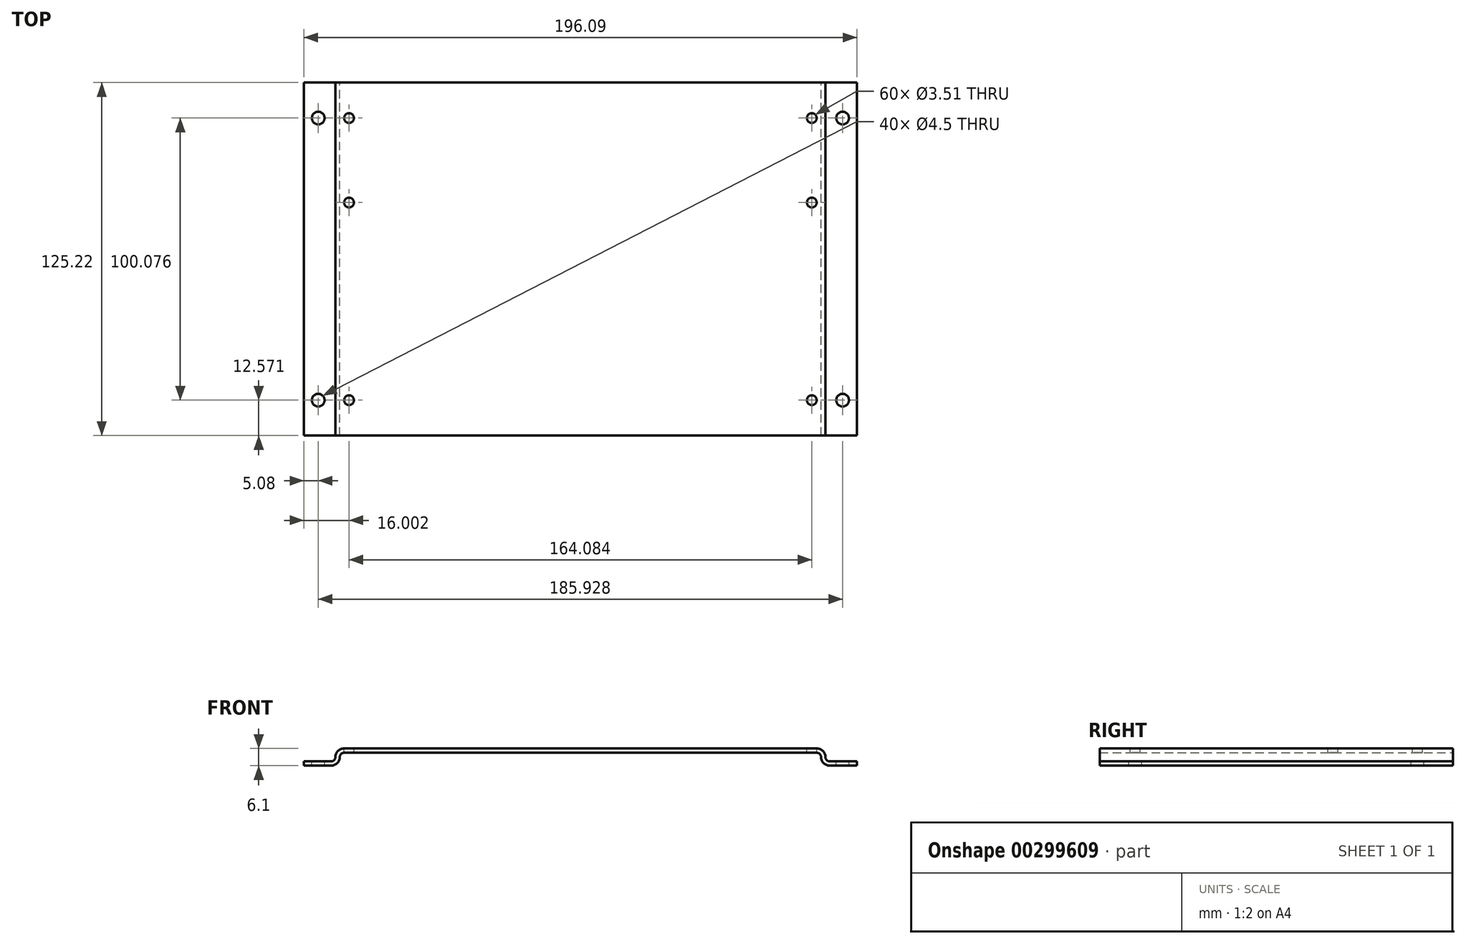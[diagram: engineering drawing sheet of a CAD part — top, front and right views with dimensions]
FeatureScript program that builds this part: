
annotation { "Feature Type Name" : "Feature", "Feature Type Description" : "" }
export const myFeature = defineFeature(function(context is Context, id is Id, definition is map)
    precondition{}
    {
        {
            var Q0;
            Q0=qCreatedBy(makeId("Front.planeOp"),FACE);
            var sketch = newSketch(context, id + "F0", { "sketchPlane" : qUnion([Q0])});
            skLineSegment(sketch, "E0.bottom", {"start": v(0, 0) * mm, "end": v(9.65, 0) * mm});
            skLineSegment(sketch, "E0.top", {"start": v(14.22, 6.1) * mm, "end": v(181.86, 6.1) * mm});
            skLineSegment(sketch, "E0.left", {"start": v(0, 0) * mm, "end": v(0, 1.52) * mm});
            skLineSegment(sketch, "E0.right", {"start": v(196.09, 0) * mm, "end": v(196.09, 1.52) * mm});
            skLineSegment(sketch, "E1", {"start": v(0, 1.52) * mm, "end": v(9.65, 1.52) * mm});
            skLineSegment(sketch, "E2", {"start": v(11.18, 3.05) * mm, "end": v(11.18, 3.05) * mm});
            skLineSegment(sketch, "E3", {"start": v(12.7, 3.05) * mm, "end": v(12.7, 3.05) * mm});
            skLineSegment(sketch, "E4", {"start": v(14.22, 4.57) * mm, "end": v(181.86, 4.57) * mm});
            skLineSegment(sketch, "E5", {"start": v(183.39, 3.05) * mm, "end": v(183.39, 3.05) * mm});
            skLineSegment(sketch, "E6", {"start": v(184.91, 3.05) * mm, "end": v(184.91, 3.05) * mm});
            skPoint(sketch, "E6.endSnap0", {"position": v(183.39, 2.29) * mm});
            skLineSegment(sketch, "E7", {"start": v(186.44, 1.52) * mm, "end": v(196.09, 1.52) * mm});
            skLineSegment(sketch, "E8.trimOffspring", {"start": v(186.44, 0) * mm, "end": v(196.09, 0) * mm});
            skPoint(sketch, "E9.visualSharp", {"position": v(12.7, 4.57) * mm});
            skArc(sketch, "E9.filletArc", {"start": v(14.22, 4.57) * mm, "mid": v(13.15, 4.13) * mm, "end": v(12.7, 3.05) * mm});
            skPoint(sketch, "E10.visualSharp", {"position": v(11.18, 1.52) * mm});
            skArc(sketch, "E10.filletArc", {"start": v(9.65, 1.52) * mm, "mid": v(10.73, 1.97) * mm, "end": v(11.18, 3.05) * mm});
            skPoint(sketch, "E11.visualSharp", {"position": v(184.91, 1.52) * mm});
            skArc(sketch, "E11.filletArc", {"start": v(184.91, 3.05) * mm, "mid": v(185.36, 1.97) * mm, "end": v(186.44, 1.52) * mm});
            skPoint(sketch, "E12.visualSharp", {"position": v(183.39, 4.57) * mm});
            skArc(sketch, "E12.filletArc", {"start": v(183.39, 3.05) * mm, "mid": v(182.94, 4.13) * mm, "end": v(181.86, 4.57) * mm});
            skPoint(sketch, "E13.visualSharp", {"position": v(184.91, 6.1) * mm});
            skArc(sketch, "E13.filletArc", {"start": v(184.91, 3.05) * mm, "mid": v(184.02, 5.2) * mm, "end": v(181.86, 6.1) * mm});
            skPoint(sketch, "E14.visualSharp", {"position": v(183.39, 0) * mm});
            skArc(sketch, "E14.filletArc", {"start": v(183.39, 3.05) * mm, "mid": v(184.28, 0.9) * mm, "end": v(186.44, 0) * mm});
            skPoint(sketch, "E15.visualSharp", {"position": v(12.7, 0) * mm});
            skArc(sketch, "E15.filletArc", {"start": v(9.65, 0) * mm, "mid": v(11.8, 0.9) * mm, "end": v(12.7, 3.05) * mm});
            skPoint(sketch, "E16.visualSharp", {"position": v(11.18, 6.1) * mm});
            skArc(sketch, "E16.filletArc", {"start": v(14.22, 6.1) * mm, "mid": v(12.07, 5.2) * mm, "end": v(11.18, 3.05) * mm});
            skSolve(sketch);
        }
        {
            var Q0;
            Q0=makeQuery(id+"F0.imprint","IMPRINT",FACE,{"disambiguationData":[TD([[makeQuery(id+"F0.imprint","IMPRINT",EDGE,{"derivedFrom":sQuery(id+"F0.wireOp",EDGE,"E0.bottom")}),1.0]])]});
            extrude(context, id + "F1", {"entities" : qUnion([Q0]), "depth" : 125.22 * mm});
        }
        {
            var Q0;
            Q0=makeQuery(id+"F1.opExtrude","SWEPT_FACE",FACE,{"disambiguationData":[OSD([sQuery(id+"F0.wireOp",EDGE,"E7")])]});
            var sketch = newSketch(context, id + "F2", { "sketchPlane" : qUnion([Q0])});
            skLineSegment(sketch, "E17", {"start": v(217.33, -62.61) * mm, "end": v(-13.47, -62.61) * mm, "construction": true});
            skPoint(sketch, "E17.startSnap0", {"position": v(196.09, -62.61) * mm});
            skLineSegment(sketch, "E18", {"start": v(98.04, -147.2) * mm, "end": v(98.04, 19.22) * mm, "construction": true});
            skCircle(sketch, "E19", {"center": v(5.08, -12.57) * mm, "radius": 2.25 * mm});
            skCircle(sketch, "E20", {"center": v(5.08, -112.65) * mm, "radius": 2.25 * mm});
            skCircle(sketch, "E21", {"center": v(191, -112.65) * mm, "radius": 2.25 * mm});
            skCircle(sketch, "E22", {"center": v(191, -12.57) * mm, "radius": 2.25 * mm});
            skSolve(sketch);
        }
        {
            var Q0;
            Q0=makeQuery(id+"F2.imprint","IMPRINT",FACE,{"disambiguationData":[TD([[makeQuery(id+"F2.imprint","IMPRINT",EDGE,{"derivedFrom":sQuery(id+"F2.wireOp",EDGE,"E20")}),1.0]])]});
            var Q1;
            Q1=makeQuery(id+"F2.imprint","IMPRINT",FACE,{"disambiguationData":[TD([[makeQuery(id+"F2.imprint","IMPRINT",EDGE,{"derivedFrom":sQuery(id+"F2.wireOp",EDGE,"E21")}),1.0]])]});
            var Q2;
            Q2=makeQuery(id+"F2.imprint","IMPRINT",FACE,{"disambiguationData":[TD([[makeQuery(id+"F2.imprint","IMPRINT",EDGE,{"derivedFrom":sQuery(id+"F2.wireOp",EDGE,"E22")}),1.0]])]});
            var Q3;
            Q3=makeQuery(id+"F2.imprint","IMPRINT",FACE,{"disambiguationData":[TD([[makeQuery(id+"F2.imprint","IMPRINT",EDGE,{"derivedFrom":sQuery(id+"F2.wireOp",EDGE,"E19")}),1.0]])]});
            extrude(context, id + "F3", {"entities" : qUnion([Q0, Q1, Q2, Q3]), "operationType" : NewBodyOperationType.REMOVE, "endBound" : BoundingType.THROUGH_ALL, "oppositeDirection" : true, "depth" : 25.4 * mm});
        }
        {
            var Q0;
            Q0=makeQuery(id+"F1.opExtrude","SWEPT_FACE",FACE,{"disambiguationData":[OSD([sQuery(id+"F0.wireOp",EDGE,"E0.top")])]});
            var sketch = newSketch(context, id + "F4", { "sketchPlane" : qUnion([Q0])});
            skCircle(sketch, "E23", {"center": v(16, -112.65) * mm, "radius": 1.75 * mm});
            skCircle(sketch, "E24", {"center": v(16, -42.55) * mm, "radius": 1.75 * mm});
            skCircle(sketch, "E25", {"center": v(16, -12.57) * mm, "radius": 1.75 * mm});
            skCircle(sketch, "E26", {"center": v(180.09, -12.57) * mm, "radius": 1.75 * mm});
            skCircle(sketch, "E27", {"center": v(180.09, -42.54) * mm, "radius": 1.75 * mm});
            skCircle(sketch, "E28", {"center": v(180.09, -112.65) * mm, "radius": 1.75 * mm});
            skLineSegment(sketch, "E29", {"start": v(98.04, -138.31) * mm, "end": v(98.04, 13.1) * mm, "construction": true});
            skSolve(sketch);
        }
        {
            var Q0;
            Q0=makeQuery(id+"F4.imprint","IMPRINT",FACE,{"disambiguationData":[TD([[makeQuery(id+"F4.imprint","IMPRINT",EDGE,{"derivedFrom":sQuery(id+"F4.wireOp",EDGE,"E25")}),1.0]])]});
            var Q1;
            Q1=makeQuery(id+"F4.imprint","IMPRINT",FACE,{"disambiguationData":[TD([[makeQuery(id+"F4.imprint","IMPRINT",EDGE,{"derivedFrom":sQuery(id+"F4.wireOp",EDGE,"E24")}),1.0]])]});
            var Q2;
            Q2=makeQuery(id+"F4.imprint","IMPRINT",FACE,{"disambiguationData":[TD([[makeQuery(id+"F4.imprint","IMPRINT",EDGE,{"derivedFrom":sQuery(id+"F4.wireOp",EDGE,"E23")}),1.0]])]});
            var Q3;
            Q3=makeQuery(id+"F4.imprint","IMPRINT",FACE,{"disambiguationData":[TD([[makeQuery(id+"F4.imprint","IMPRINT",EDGE,{"derivedFrom":sQuery(id+"F4.wireOp",EDGE,"E28")}),1.0]])]});
            var Q4;
            Q4=makeQuery(id+"F4.imprint","IMPRINT",FACE,{"disambiguationData":[TD([[makeQuery(id+"F4.imprint","IMPRINT",EDGE,{"derivedFrom":sQuery(id+"F4.wireOp",EDGE,"E27")}),1.0]])]});
            var Q5;
            Q5=makeQuery(id+"F4.imprint","IMPRINT",FACE,{"disambiguationData":[TD([[makeQuery(id+"F4.imprint","IMPRINT",EDGE,{"derivedFrom":sQuery(id+"F4.wireOp",EDGE,"E26")}),1.0]])]});
            extrude(context, id + "F5", {"entities" : qUnion([Q0, Q1, Q2, Q3, Q4, Q5]), "operationType" : NewBodyOperationType.REMOVE, "oppositeDirection" : true, "depth" : 25.4 * mm});
        }
    });
